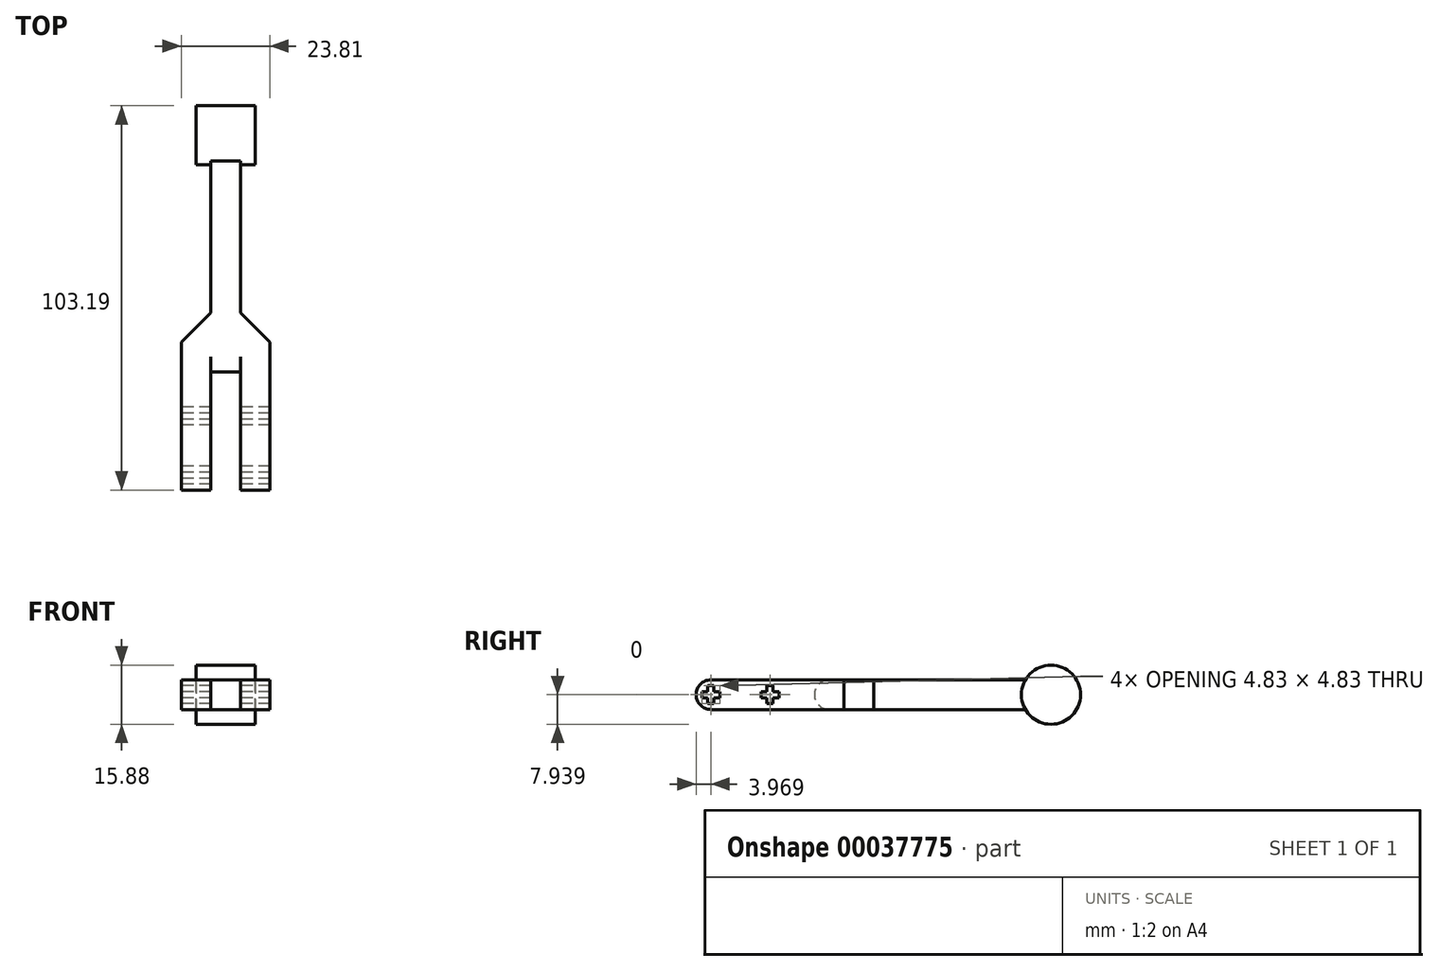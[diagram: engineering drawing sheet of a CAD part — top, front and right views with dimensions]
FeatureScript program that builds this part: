
annotation { "Feature Type Name" : "Feature", "Feature Type Description" : "" }
export const myFeature = defineFeature(function(context is Context, id is Id, definition is map)
    precondition{}
    {
        {
            var Q0;
            Q0=qCreatedBy(makeId("Top.planeOp"),FACE);
            var sketch = newSketch(context, id + "F0", { "sketchPlane" : qUnion([Q0])});
            skLineSegment(sketch, "E0.bottom", {"start": v(0, 0) * mm, "end": v(7.94, 0) * mm});
            skLineSegment(sketch, "E0.left", {"start": v(0, 0) * mm, "end": v(0, 39.69) * mm});
            skLineSegment(sketch, "E0.right", {"start": v(7.94, 0) * mm, "end": v(7.94, 31.75) * mm});
            skLineSegment(sketch, "E1.bottom", {"start": v(15.88, 0) * mm, "end": v(23.81, 0) * mm});
            skLineSegment(sketch, "E1.left", {"start": v(15.88, 0) * mm, "end": v(15.88, 31.75) * mm});
            skLineSegment(sketch, "E1.right", {"start": v(23.81, 0) * mm, "end": v(23.81, 39.69) * mm});
            skLineSegment(sketch, "E2", {"start": v(7.94, 31.75) * mm, "end": v(15.87, 31.75) * mm});
            skLineSegment(sketch, "E3", {"start": v(0, 39.69) * mm, "end": v(7.94, 39.69) * mm});
            skLineSegment(sketch, "E4", {"start": v(7.94, 39.69) * mm, "end": v(7.94, 87.31) * mm});
            skLineSegment(sketch, "E5", {"start": v(7.94, 87.31) * mm, "end": v(15.88, 87.31) * mm});
            skLineSegment(sketch, "E6", {"start": v(15.87, 87.31) * mm, "end": v(15.87, 39.69) * mm});
            skLineSegment(sketch, "E7", {"start": v(15.88, 39.69) * mm, "end": v(23.81, 39.69) * mm});
            skLineSegment(sketch, "E8", {"start": v(7.94, 39.69) * mm, "end": v(15.88, 39.69) * mm, "construction": true});
            skLineSegment(sketch, "E9", {"start": v(11.9, 39.69) * mm, "end": v(11.9, 31.75) * mm, "construction": true});
            skSolve(sketch);
        }
        {
            var Q0;
            Q0=qSketchRegion(id+"F0",true);
            extrude(context, id + "F1", {"entities" : qUnion([Q0]), "depth" : 7.94 * mm});
        }
        {
            var Q0;
            Q0=makeQuery(id+"F1.opExtrude","CAP_EDGE",EDGE,{"disambiguationData":[OSD([sQuery(id+"F0.wireOp",EDGE,"E0.bottom")])],"isStart":true});
            var Q1;
            Q1=makeQuery(id+"F1.opExtrude","CAP_EDGE",EDGE,{"disambiguationData":[OSD([sQuery(id+"F0.wireOp",EDGE,"E0.bottom")])],"isStart":false});
            var Q2;
            Q2=makeQuery(id+"F1.opExtrude","CAP_EDGE",EDGE,{"disambiguationData":[OSD([sQuery(id+"F0.wireOp",EDGE,"E1.bottom")])],"isStart":false});
            var Q3;
            Q3=makeQuery(id+"F1.opExtrude","CAP_EDGE",EDGE,{"disambiguationData":[OSD([sQuery(id+"F0.wireOp",EDGE,"E1.bottom")])],"isStart":true});
            var Q4;
            Q4=makeQuery(id+"F1.opExtrude","CAP_EDGE",EDGE,{"disambiguationData":[OSD([sQuery(id+"F0.wireOp",EDGE,"E2")])],"isStart":false});
            var Q5;
            Q5=makeQuery(id+"F1.opExtrude","CAP_EDGE",EDGE,{"disambiguationData":[OSD([sQuery(id+"F0.wireOp",EDGE,"E2")])],"isStart":true});
            fillet(context, id + "F2", {"entities" : qUnion([Q0, Q1, Q2, Q3, Q4, Q5]), "radius" : 3.97 * mm, "tangentPropagation" : true, "allowEdgeOverflow" : false});
        }
        {
            var Q0;
            Q0=makeQuery(id+"FNYOd53glhffsHS_1.boolean.opBoolean","MERGE",FACE,{"derivedFrom":[makeQuery(id+"F1.opExtrude","SWEPT_FACE",FACE,{"disambiguationData":[OSD([sQuery(id+"F0.wireOp",EDGE,"E0.left")])]}),makeQuery(id+"FNYOd53glhffsHS_1.opExtrude","SWEPT_FACE",FACE,{"disambiguationData":[OSD([sQuery(id+"F2h7VdxgF09O83Z_1.wireOp",EDGE,"9d81e400-ffae-42b2-a3b4-f3f00290e241.left")])]})]});
            var sketch = newSketch(context, id + "F3", { "sketchPlane" : qUnion([Q0])});
            skLineSegment(sketch, "E10.rect.bottom", {"start": v(-1.56, 3.12) * mm, "end": v(-6.38, 3.12) * mm});
            skLineSegment(sketch, "E10.rect.top", {"start": v(-1.56, 4.81) * mm, "end": v(-6.38, 4.81) * mm});
            skLineSegment(sketch, "E10.rect.left", {"start": v(-1.56, 3.12) * mm, "end": v(-1.56, 4.81) * mm});
            skLineSegment(sketch, "E10.rect.right", {"start": v(-6.38, 3.12) * mm, "end": v(-6.38, 4.81) * mm});
            skPoint(sketch, "E10.rect.middle", {"position": v(-3.97, 3.97) * mm});
            skLineSegment(sketch, "E11.rect.bottom", {"start": v(-4.81, 6.38) * mm, "end": v(-3.12, 6.38) * mm});
            skLineSegment(sketch, "E11.rect.top", {"start": v(-4.81, 1.56) * mm, "end": v(-3.12, 1.56) * mm});
            skLineSegment(sketch, "E11.rect.left", {"start": v(-4.81, 6.38) * mm, "end": v(-4.81, 1.56) * mm});
            skLineSegment(sketch, "E11.rect.right", {"start": v(-3.12, 6.38) * mm, "end": v(-3.12, 1.56) * mm});
            skLineSegment(sketch, "E12", {"start": v(-3.97, 3.97) * mm, "end": v(-19.84, 3.97) * mm, "construction": true});
            skLineSegment(sketch, "E13.rect.bottom", {"start": v(-20.69, 1.56) * mm, "end": v(-19, 1.56) * mm});
            skLineSegment(sketch, "E13.rect.top", {"start": v(-20.69, 6.38) * mm, "end": v(-19, 6.38) * mm});
            skLineSegment(sketch, "E13.rect.left", {"start": v(-20.69, 1.56) * mm, "end": v(-20.69, 6.38) * mm});
            skLineSegment(sketch, "E13.rect.right", {"start": v(-19, 1.56) * mm, "end": v(-19, 6.38) * mm});
            skPoint(sketch, "E13.rect.middle", {"position": v(-19.84, 3.97) * mm});
            skLineSegment(sketch, "E14.rect.bottom", {"start": v(-22.26, 4.81) * mm, "end": v(-17.43, 4.81) * mm});
            skLineSegment(sketch, "E14.rect.top", {"start": v(-22.26, 3.12) * mm, "end": v(-17.43, 3.12) * mm});
            skLineSegment(sketch, "E14.rect.left", {"start": v(-22.26, 4.81) * mm, "end": v(-22.26, 3.12) * mm});
            skLineSegment(sketch, "E14.rect.right", {"start": v(-17.43, 4.81) * mm, "end": v(-17.43, 3.12) * mm});
            skSolve(sketch);
        }
        {
            var Q0;
            Q0=qSketchRegion(id+"F3",true);
            var Q1;
            Q1=makeQuery(id+"FNYOd53glhffsHS_1.boolean.opBoolean","MERGE",FACE,{"derivedFrom":[makeQuery(id+"F1.opExtrude","SWEPT_FACE",FACE,{"disambiguationData":[OSD([sQuery(id+"F0.wireOp",EDGE,"E1.right")])]}),makeQuery(id+"FNYOd53glhffsHS_1.opExtrude","SWEPT_FACE",FACE,{"disambiguationData":[OSD([sQuery(id+"F2h7VdxgF09O83Z_1.wireOp",EDGE,"894c2ef8-1dbc-4df3-bad7-f21cdf97773c.left")])]})]});
            extrude(context, id + "F4", {"entities" : qUnion([Q0]), "operationType" : NewBodyOperationType.REMOVE, "endBound" : BoundingType.UP_TO_SURFACE, "oppositeDirection" : true, "endBoundEntityFace" : qUnion([Q1]), "depth" : 25.4 * mm});
        }
        {
            var Q0;
            Q0=makeQuery(id+"F1.opExtrude","SWEPT_EDGE",EDGE,{"disambiguationData":[OSD([sQuery(id+"F0.wireOp",EDGE,"E3"),sQuery(id+"F0.wireOp",EDGE,"E4")])]});
            var Q1;
            Q1=makeQuery(id+"F1.opExtrude","SWEPT_EDGE",EDGE,{"disambiguationData":[OSD([sQuery(id+"F0.wireOp",EDGE,"E6"),sQuery(id+"F0.wireOp",EDGE,"E7")])]});
            chamfer(context, id + "F5", {"entities" : qUnion([Q0, Q1]), "width" : 7.94 * mm, "tangentPropagation" : true});
        }
        {
            var Q0;
            Q0=makeQuery(id+"F1.opExtrude","SWEPT_FACE",FACE,{"disambiguationData":[OSD([sQuery(id+"F0.wireOp",EDGE,"E5")])]});
            var sketch = newSketch(context, id + "F6", { "sketchPlane" : qUnion([Q0])});
            skLineSegment(sketch, "E15", {"start": v(-11.9, 7.94) * mm, "end": v(-11.9, 0) * mm, "construction": true});
            skLineSegment(sketch, "E16.rect.bottom", {"start": v(-3.97, 11.9) * mm, "end": v(-19.84, 11.9) * mm});
            skLineSegment(sketch, "E16.rect.top", {"start": v(-3.97, -3.97) * mm, "end": v(-19.84, -3.97) * mm});
            skLineSegment(sketch, "E16.rect.left", {"start": v(-3.97, 11.9) * mm, "end": v(-3.97, -3.97) * mm});
            skLineSegment(sketch, "E16.rect.right", {"start": v(-19.84, 11.9) * mm, "end": v(-19.84, -3.97) * mm});
            skPoint(sketch, "E16.rect.middle", {"position": v(-11.9, 3.97) * mm});
            skSolve(sketch);
        }
        {
            var Q0;
            Q0 = qSketchRegion(id + "F6", true);
            extrude(context, id + "F7", {"entities" : qUnion([Q0]), "operationType" : NewBodyOperationType.ADD, "depth" : 15.88 * mm});
        }
        {
            var Q0;
            Q0=makeQuery(id+"F7.opExtrude","CAP_EDGE",EDGE,{"disambiguationData":[OSD([sQuery(id+"F6.wireOp",EDGE,"E16.rect.top")])],"isStart":true});
            var Q1;
            Q1=makeQuery(id+"F7.opExtrude","CAP_EDGE",EDGE,{"disambiguationData":[OSD([sQuery(id+"F6.wireOp",EDGE,"E16.rect.bottom")])],"isStart":true});
            var Q2;
            Q2=makeQuery(id+"F7.opExtrude","CAP_EDGE",EDGE,{"disambiguationData":[OSD([sQuery(id+"F6.wireOp",EDGE,"E16.rect.top")])],"isStart":false});
            var Q3;
            Q3=makeQuery(id+"F7.opExtrude","CAP_EDGE",EDGE,{"disambiguationData":[OSD([sQuery(id+"F6.wireOp",EDGE,"E16.rect.bottom")])],"isStart":false});
            fillet(context, id + "F8", {"entities" : qUnion([Q0, Q1, Q2, Q3]), "radius" : 7.94 * mm, "tangentPropagation" : true, "allowEdgeOverflow" : false});
        }
    });
